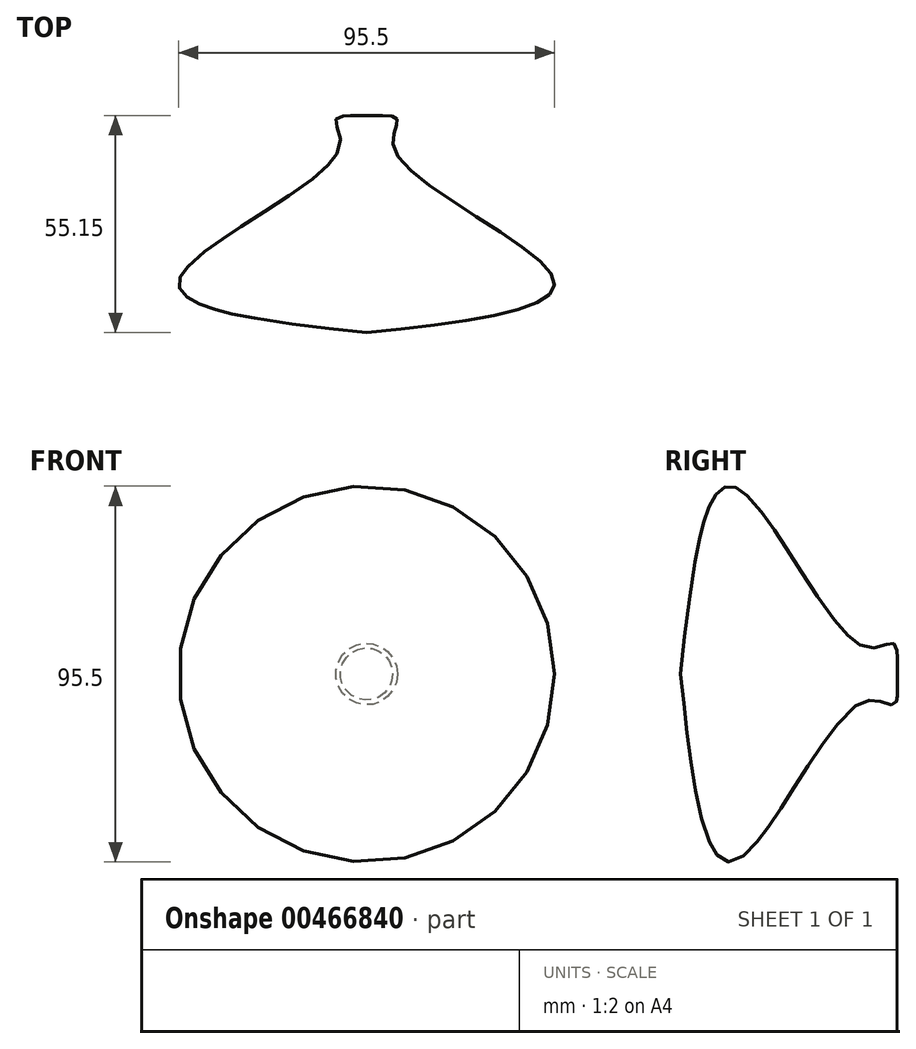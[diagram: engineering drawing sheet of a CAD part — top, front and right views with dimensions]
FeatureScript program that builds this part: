
annotation { "Feature Type Name" : "Feature", "Feature Type Description" : "" }
export const myFeature = defineFeature(function(context is Context, id is Id, definition is map)
    precondition{}
    {
        {
            var Q0;
            Q0=qCreatedBy(makeId("Top.planeOp"),FACE);
            var sketch = newSketch(context, id + "F0", { "sketchPlane" : qUnion([Q0])});
            skLineSegment(sketch, "E0", {"start": v(0, 0) * mm, "end": v(0, 54.97) * mm});
            skFitSpline(sketch, "E1", {"points": [v(0, 0) * mm, v(47.49, 13.81) * mm, v(7.2, 46.05) * mm, v(7.77, 54.1) * mm, v(0, 54.97) * mm], "startDerivative": vector(214.28, 23.28) * mm, "endDerivative": vector(-77.6, -4.99) * mm});
            skArc(sketch, "E2", {"start": v(0, 0) * mm, "mid": v(0.04, -1.43) * mm, "end": v(0.16, -2.86) * mm});
            skArc(sketch, "E3", {"start": v(25.36, 0) * mm, "mid": v(12.45, 1.36) * mm, "end": v(0.16, -2.86) * mm});
            skLineSegment(sketch, "E4", {"start": v(25.36, 0) * mm, "end": v(0, 0) * mm});
            skSolve(sketch);
        }
        {
            var Q0;
            Q0=makeQuery(id+"F0.imprint","IMPRINT",FACE,{"disambiguationData":[TD([[makeQuery(id+"F0.imprint","IMPRINT",EDGE,{"derivedFrom":sQuery(id+"F0.wireOp",EDGE,"E0")}),-1.0]])]});
            var Q1;
            Q1=sQuery(id+"F0.wireOp",EDGE,"E0");
            revolve(context, id + "F1", {"entities" : qUnion([Q0]), "axis" : qUnion([Q1]), "revolveType" : RevolveType.FULL});
        }
    });
